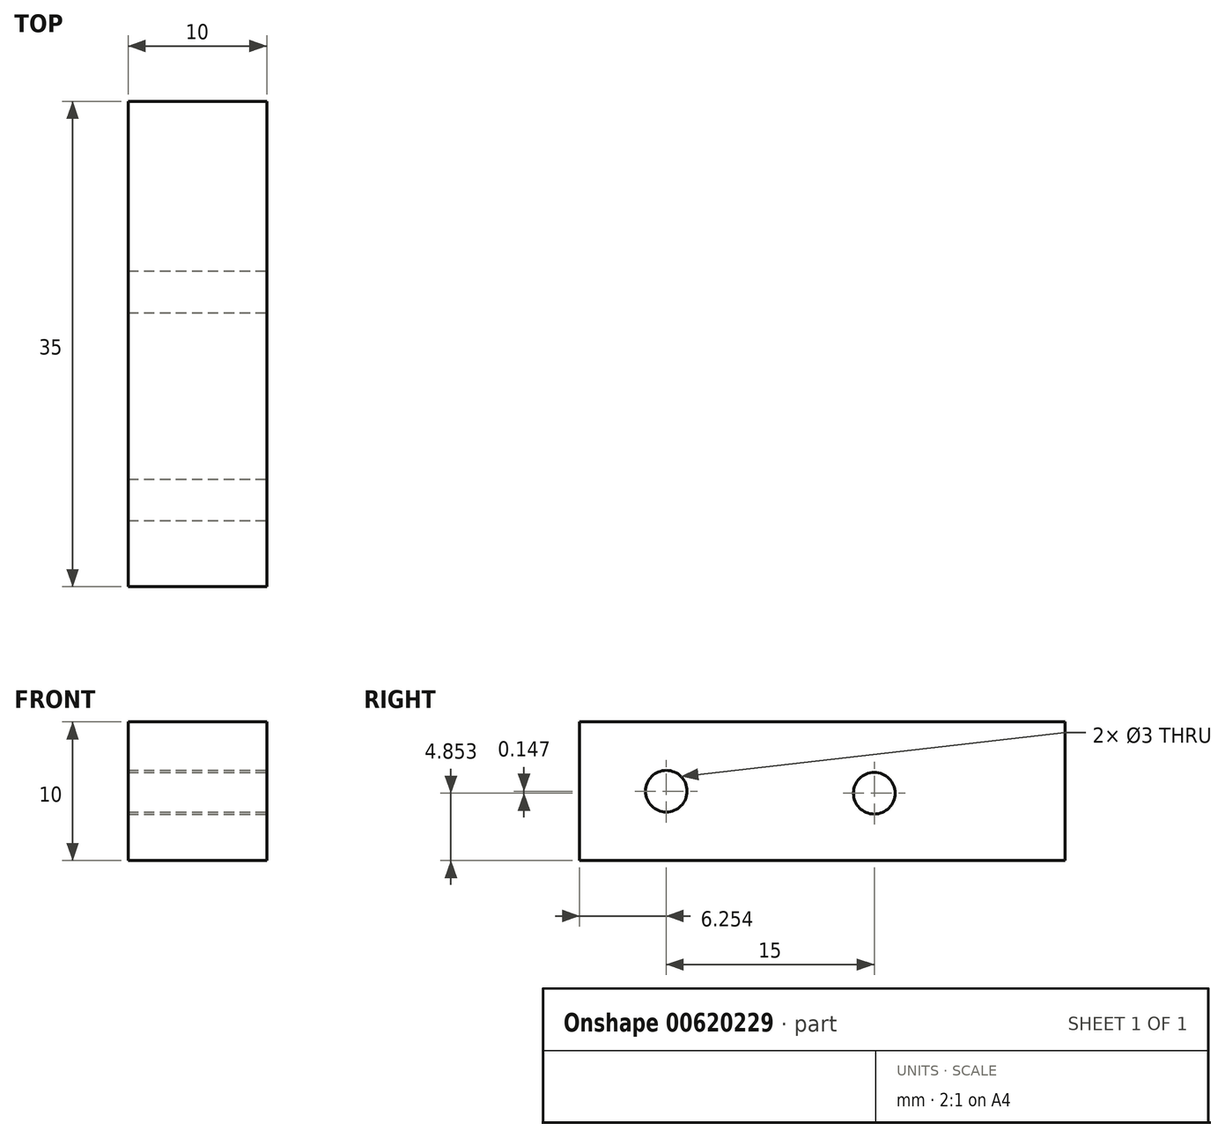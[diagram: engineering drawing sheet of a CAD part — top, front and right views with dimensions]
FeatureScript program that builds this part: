
annotation { "Feature Type Name" : "Feature", "Feature Type Description" : "" }
export const myFeature = defineFeature(function(context is Context, id is Id, definition is map)
    precondition{}
    {
        {
            var Q0;
            Q0=qCreatedBy(makeId("Front.planeOp"),FACE);
            var sketch = newSketch(context, id + "F0", { "sketchPlane" : qUnion([Q0])});
            skLineSegment(sketch, "E0.bottom", {"start": v(0, 0) * mm, "end": v(-10, 0) * mm});
            skLineSegment(sketch, "E0.top", {"start": v(0, 10) * mm, "end": v(-10, 10) * mm});
            skLineSegment(sketch, "E0.left", {"start": v(0, 0) * mm, "end": v(0, 10) * mm});
            skLineSegment(sketch, "E0.right", {"start": v(-10, 0) * mm, "end": v(-10, 10) * mm});
            skSolve(sketch);
        }
        {
            var Q0;
            Q0 = qSketchRegion(id + "F0", true);
            extrude(context, id + "F1", {"entities" : qUnion([Q0]), "depth" : 35 * mm, "offsetDistance" : 25 * mm});
        }
        {
            var Q0;
            Q0=makeQuery(id+"F1.opExtrude","SWEPT_FACE",FACE,{"disambiguationData":[OSD([sQuery(id+"F0.wireOp",EDGE,"E0.left")])]});
            var sketch = newSketch(context, id + "F2", { "sketchPlane" : qUnion([Q0])});
            skCircle(sketch, "E1", {"center": v(-28.75, 5) * mm, "radius": 1.5 * mm});
            skPoint(sketch, "E1.centerSnap0", {"position": v(-35, 5) * mm});
            skCircle(sketch, "E2", {"center": v(-13.75, 4.85) * mm, "radius": 1.5 * mm});
            skSolve(sketch);
        }
        {
            var Q0;
            Q0 = qSketchRegion(id + "F2", true);
            extrude(context, id + "F3", {"entities" : qUnion([Q0]), "operationType" : NewBodyOperationType.REMOVE, "oppositeDirection" : true, "depth" : 12 * mm, "offsetDistance" : 25 * mm});
        }
    });
